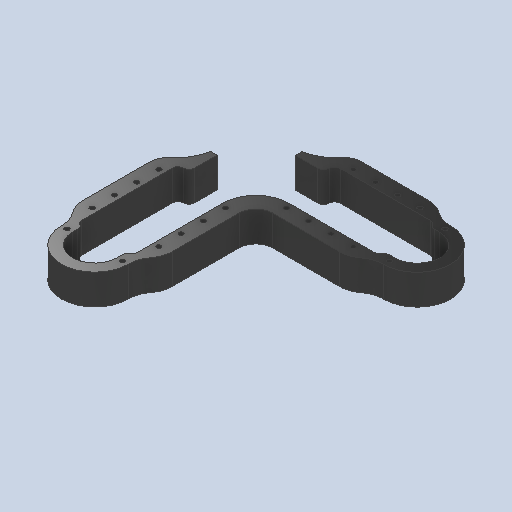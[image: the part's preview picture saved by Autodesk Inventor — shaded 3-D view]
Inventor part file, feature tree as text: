
AUTODESK INVENTOR PART (.ipt)
format: ipt  version: 2025.1 (Build 291241020, 241B)  size: 295,936 bytes
history: native  units: in
note: dims shown in document units (in); Inventor stores cm internally (conversion verified against a paired STEP export)
features: plane x1, extrude x1, sketch x1
ambient origin geometry x8: Origin, YZ Plane, XZ Plane, XY Plane, X Axis, Y Axis, Z Axis, Center Point
bodies: Solid1 (feature_tree)
feature tree (3):
  plane  "Work Plane1"
  extrude  "Extrusion2"  Depth=0.25in
  sketch  "Sketch2"  dims[d55=1.355in d56=0.0in d62=0.2087in d64=0.2832in d65=1.0084in d72=0.5in d73=0.75in d74=0.75in d75=0.2528in d76=1.0in d77=1.0in d78=1.0in d104=0.25in d105=0.25in d106=0.25in d107=0.25in d109=0.25in d110=0.25in d111=0.75in d112=0.75in d114=1.375in d115=1.25in d116=1.0in d117=1.0in d118=1.0in d122=1.5in d124=0.2087in d125=0.25in d126=0.25in d127=0.25in d128=0.2357in d129=0.5in d130=0.75in d131=0.75in d132=0.6687in d133=0.25in d134=3.817in d135=0.2165in d136=1.0in d137=4.0379in d138=11.282in d139=1.0in d140=0.2357in d141=0.5in d142=0.5in d143=0.75in d144=0.75in d145=0.5in d146=1.0in d147=0.75in d148=1.0in d149=1.0in d150=1.0in d151=0.2087in d152=0.75in d153=0.4999in d154=0.75in d155=1.5043in d156=1.0042in d157=0.25in d158=0.25in d159=3.8254in d160=0.433in d161=0.2165in d162=0.2357in d163=0.2087in d164=1.5048in d165=0.2357in d166=0.25in d167=0.25in d168=0.433in d169=0.2087in d170=0.2087in d171=1.8433in d172=1.0084in d173=2.0in d174=0.75in d175=0.5769in d176=2.9857in d177=0.2087in d178=0.2087in d179=0.433in d180=0.2165in d181=0.125in d182=2.9857in d183=4.067in d184=0.2832in d185=1.0084in d186=2.0in d187=0.75in d188=0.25in d189=1.1798in d190=0.5655in d191=0.1898in]
